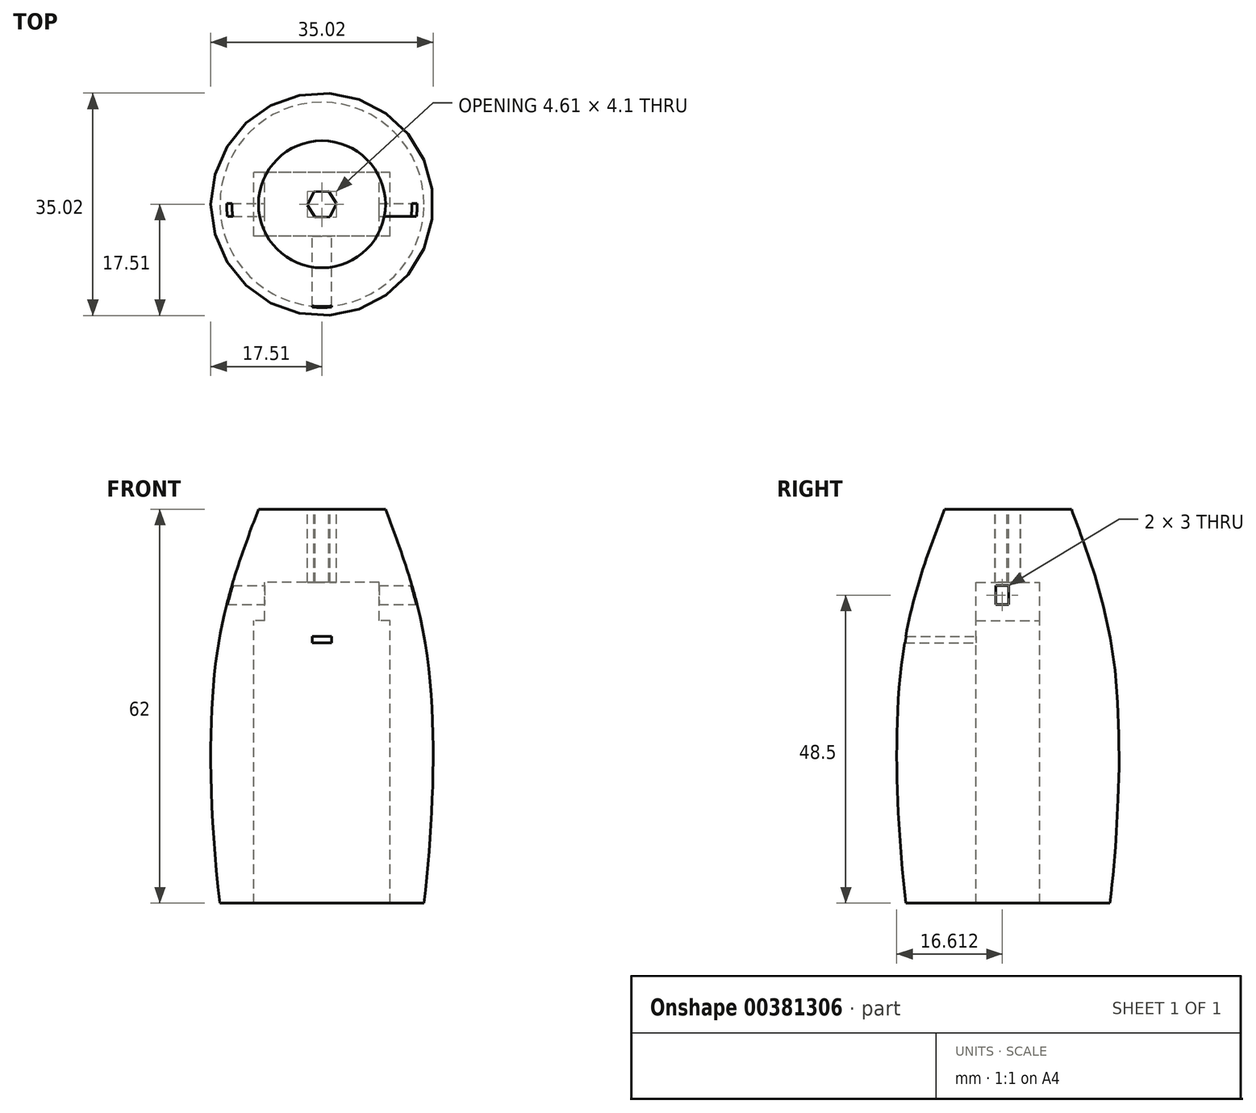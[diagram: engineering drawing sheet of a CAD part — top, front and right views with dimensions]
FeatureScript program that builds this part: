
annotation { "Feature Type Name" : "Feature", "Feature Type Description" : "" }
export const myFeature = defineFeature(function(context is Context, id is Id, definition is map)
    precondition{}
    {
        {
            var Q0;
            Q0=qCreatedBy(makeId("Front.planeOp"),FACE);
            var sketch = newSketch(context, id + "F0", { "sketchPlane" : qUnion([Q0])});
            skLineSegment(sketch, "E0.bottom", {"start": v(10.75, -19.5) * mm, "end": v(-10.75, -19.5) * mm});
            skLineSegment(sketch, "E0.top", {"start": v(10.75, 44.5) * mm, "end": v(9, 44.5) * mm});
            skLineSegment(sketch, "E0.left", {"start": v(10.75, -19.5) * mm, "end": v(10.75, 44.5) * mm});
            skLineSegment(sketch, "E0.right", {"start": v(-10.75, -19.5) * mm, "end": v(-10.75, 44.5) * mm});
            skPoint(sketch, "E0.middle", {"position": v(0, 12.5) * mm});
            skLineSegment(sketch, "E1", {"start": v(-10.75, 0) * mm, "end": v(10.75, 0) * mm, "construction": true});
            skLineSegment(sketch, "E2.top", {"start": v(9, 50.5) * mm, "end": v(-9, 50.5) * mm});
            skLineSegment(sketch, "E2.left", {"start": v(9, 44.5) * mm, "end": v(9, 50.5) * mm});
            skLineSegment(sketch, "E2.right", {"start": v(-9, 44.5) * mm, "end": v(-9, 50.5) * mm});
            skPoint(sketch, "E2.middle", {"position": v(0, 47.5) * mm});
            skPoint(sketch, "E2.middle.positionSnap0", {"position": v(0, 44.5) * mm});
            skPoint(sketch, "E2.centerSnap0", {"position": v(0, 44.5) * mm});
            skLineSegment(sketch, "E3.trimOffspring", {"start": v(-9, 44.5) * mm, "end": v(-10.75, 44.5) * mm});
            skSolve(sketch);
        }
        {
            var Q0;
            Q0=qCreatedBy(makeId("Front.planeOp"),FACE);
            var sketch = newSketch(context, id + "F1", { "sketchPlane" : qUnion([Q0])});
            skLineSegment(sketch, "E4", {"start": v(0, 0) * mm, "end": v(0, 25) * mm, "construction": true});
            skLineSegment(sketch, "E5", {"start": v(-17.5, 25) * mm, "end": v(17.5, 25) * mm, "construction": true});
            skLineSegment(sketch, "E6", {"start": v(-15, 47) * mm, "end": v(-2, 47) * mm, "construction": true});
            skPoint(sketch, "E7", {"position": v(0, 47) * mm});
            skPoint(sketch, "E8", {"position": v(0, -19.5) * mm});
            skLineSegment(sketch, "E9", {"start": v(-12.5, -19.5) * mm, "end": v(-1.25, -19.5) * mm, "construction": true});
            skLineSegment(sketch, "E10", {"start": v(0, -19.5) * mm, "end": v(0, -49.5) * mm, "construction": true});
            skLineSegment(sketch, "E11", {"start": v(0, 47) * mm, "end": v(0, 62) * mm, "construction": true});
            skLineSegment(sketch, "E12", {"start": v(-10, 62) * mm, "end": v(-2, 62) * mm});
            skFitSpline(sketch, "E13", {"points": [v(-10, 62) * mm, v(-15, 47) * mm, v(-17.5, 25) * mm, v(-12.5, -19.5) * mm, v(0, -49.5) * mm], "startDerivative": vector(-28.9, -76.62) * mm, "endDerivative": vector(51.56, -101.04) * mm});
            skLineSegment(sketch, "E14.0", {"start": v(-2, 50) * mm, "end": v(-2, 62) * mm});
            skPoint(sketch, "E15.orphan", {"position": v(10, 62) * mm});
            skLineSegment(sketch, "E16.0", {"start": v(-1.25, -43.05) * mm, "end": v(-1.25, -47.05) * mm});
            skLineSegment(sketch, "E17", {"start": v(0, 47) * mm, "end": v(-2, 47) * mm});
            skLineSegment(sketch, "E18", {"start": v(0, 50) * mm, "end": v(-2, 50) * mm});
            skLineSegment(sketch, "E19.trimOffspring", {"start": v(0, 47) * mm, "end": v(15, 47) * mm, "construction": true});
            skLineSegment(sketch, "E20.trimOffspring", {"start": v(0, -19.5) * mm, "end": v(12.5, -19.5) * mm, "construction": true});
            skLineSegment(sketch, "E21", {"start": v(0, 50) * mm, "end": v(0, -19.5) * mm});
            skLineSegment(sketch, "E22", {"start": v(0, -19.5) * mm, "end": v(-1.75, -19.5) * mm});
            skLineSegment(sketch, "E23", {"start": v(-1.75, -19.5) * mm, "end": v(-1.75, -43.05) * mm});
            skLineSegment(sketch, "E24", {"start": v(-1.25, -43.05) * mm, "end": v(-1.75, -43.05) * mm});
            skSolve(sketch);
        }
        {
            var Q0;
            Q0=makeQuery(id+"F1.imprint","IMPRINT",FACE,{"disambiguationData":[TD([[makeQuery(id+"F1.imprint","IMPRINT",EDGE,{"derivedFrom":sQuery(id+"F1.wireOp",EDGE,"E12")}),-1.0]])]});
            var Q1;
            Q1=sQuery(id+"F1.wireOp",EDGE,"E11");
            revolve(context, id + "F2", {"entities" : qUnion([Q0]), "axis" : qUnion([Q1]), "revolveType" : RevolveType.FULL});
        }
        {
            var Q0;
            Q0=qSketchRegion(id+"F0",true);
            extrude(context, id + "F3", {"entities" : qUnion([Q0]), "operationType" : NewBodyOperationType.REMOVE, "endBound" : BoundingType.SYMMETRIC, "depth" : 10 * mm});
        }
        {
            var Q0;
            Q0=makeQuery(id+"F2.opRevolve","SWEPT_FACE",FACE,{"disambiguationData":[OSD([sQuery(id+"F1.wireOp",EDGE,"E12")])]});
            var sketch = newSketch(context, id + "F4", { "sketchPlane" : qUnion([Q0])});
            skCircle(sketch, "E25.cCircle", {"center": v(0, 0) * mm, "radius": 2 * mm, "construction": true});
            skLineSegment(sketch, "E25.0", {"start": v(2.3, 0.1) * mm, "end": v(1.24, -1.95) * mm});
            skLineSegment(sketch, "E25.1", {"start": v(1.24, -1.95) * mm, "end": v(-1.06, -2.05) * mm});
            skLineSegment(sketch, "E25.2", {"start": v(-1.06, -2.05) * mm, "end": v(-2.3, -0.1) * mm});
            skLineSegment(sketch, "E25.3", {"start": v(-2.3, -0.1) * mm, "end": v(-1.24, 1.95) * mm});
            skLineSegment(sketch, "E25.4", {"start": v(-1.24, 1.95) * mm, "end": v(1.06, 2.05) * mm});
            skLineSegment(sketch, "E25.5", {"start": v(1.06, 2.05) * mm, "end": v(2.3, 0.1) * mm});
            skPoint(sketch, "E25.0.midPoint", {"position": v(1.77, -0.92) * mm});
            skSolve(sketch);
        }
        {
            var Q0;
            Q0=qSketchRegion(id+"F4",true);
            extrude(context, id + "F5", {"entities" : qUnion([Q0]), "operationType" : NewBodyOperationType.REMOVE, "oppositeDirection" : true, "depth" : 15 * mm});
        }
        {
            var Q0;
            Q0=qCreatedBy(makeId("Right.planeOp"),FACE);
            var sketch = newSketch(context, id + "F6", { "sketchPlane" : qUnion([Q0])});
            skLineSegment(sketch, "E26.bottom", {"start": v(0.1, 47) * mm, "end": v(-1.9, 47) * mm});
            skLineSegment(sketch, "E26.top", {"start": v(0.1, 50) * mm, "end": v(-1.9, 50) * mm});
            skLineSegment(sketch, "E26.left", {"start": v(0.1, 47) * mm, "end": v(0.1, 50) * mm});
            skLineSegment(sketch, "E26.right", {"start": v(-1.9, 47) * mm, "end": v(-1.9, 50) * mm});
            skPoint(sketch, "E26.middle", {"position": v(0, 48) * mm});
            skSolve(sketch);
        }
        {
            var Q0;
            Q0=qSketchRegion(id+"F6",true);
            extrude(context, id + "F7", {"entities" : qUnion([Q0]), "operationType" : NewBodyOperationType.REMOVE, "endBound" : BoundingType.SYMMETRIC, "oppositeDirection" : true, "depth" : 41 * mm});
        }
        {
            var Q0;
            Q0=qCreatedBy(makeId("Front.planeOp"),FACE);
            var sketch = newSketch(context, id + "F8", { "sketchPlane" : qUnion([Q0])});
            skLineSegment(sketch, "E27.bottom", {"start": v(1.5, 41) * mm, "end": v(-1.5, 41) * mm});
            skLineSegment(sketch, "E27.top", {"start": v(1.5, 42) * mm, "end": v(-1.5, 42) * mm});
            skLineSegment(sketch, "E27.left", {"start": v(1.5, 41) * mm, "end": v(1.5, 42) * mm});
            skLineSegment(sketch, "E27.right", {"start": v(-1.5, 41) * mm, "end": v(-1.5, 42) * mm});
            skPoint(sketch, "E27.middle", {"position": v(0, 41.5) * mm});
            skSolve(sketch);
        }
        {
            var Q0;
            Q0=qSketchRegion(id+"F8",true);
            extrude(context, id + "F9", {"entities" : qUnion([Q0]), "operationType" : NewBodyOperationType.REMOVE, "endBound" : BoundingType.THROUGH_ALL, "depth" : 25 * mm});
        }
        {
            var Q0;
            Q0=makeQuery(id+"F2.opRevolve","SWEPT_EDGE",EDGE,{"disambiguationData":[OSD([sQuery(id+"F1.wireOp",EDGE,"E13"),sQuery(id+"F1.wireOp",EDGE,"E16.0")])]});
            fillet(context, id + "F10", {"entities" : qUnion([Q0]), "radius" : 0.3 * mm, "tangentPropagation" : true, "allowEdgeOverflow" : false});
        }
        {
            var Q0;
            Q0=makeQuery(id+"F2.opRevolve","SWEPT_EDGE",EDGE,{"disambiguationData":[OSD([sQuery(id+"F1.wireOp",EDGE,"E16.0"),sQuery(id+"F1.wireOp",EDGE,"E24")])]});
            fillet(context, id + "F11", {"entities" : qUnion([Q0]), "radius" : 0.1 * mm, "tangentPropagation" : true, "allowEdgeOverflow" : false});
        }
        {
            var Q0;
            Q0=makeQuery(id+"F2.opRevolve","SWEPT_EDGE",EDGE,{"disambiguationData":[OSD([sQuery(id+"F1.wireOp",EDGE,"E23"),sQuery(id+"F1.wireOp",EDGE,"E24")])]});
            fillet(context, id + "F12", {"entities" : qUnion([Q0]), "radius" : 0.1 * mm, "tangentPropagation" : true, "allowEdgeOverflow" : false});
        }
        {
            var Q0;
            Q0=qCreatedBy(makeId("Top.planeOp"),FACE);
            var sketch = newSketch(context, id + "F13", { "sketchPlane" : qUnion([Q0])});
            skLineSegment(sketch, "E28.bottom", {"start": v(50, -50) * mm, "end": v(-50, -50) * mm});
            skLineSegment(sketch, "E28.top", {"start": v(50, 50) * mm, "end": v(-50, 50) * mm});
            skLineSegment(sketch, "E28.left", {"start": v(50, -50) * mm, "end": v(50, 50) * mm});
            skLineSegment(sketch, "E28.right", {"start": v(-50, -50) * mm, "end": v(-50, 50) * mm});
            skPoint(sketch, "E28.middle", {"position": v(0, 0) * mm});
            skSolve(sketch);
        }
        {
            var Q0;
            Q0=qSketchRegion(id+"F13",true);
            extrude(context, id + "F14", {"entities" : qUnion([Q0]), "operationType" : NewBodyOperationType.REMOVE, "endBound" : BoundingType.THROUGH_ALL, "oppositeDirection" : true, "depth" : 25 * mm});
        }
    });
